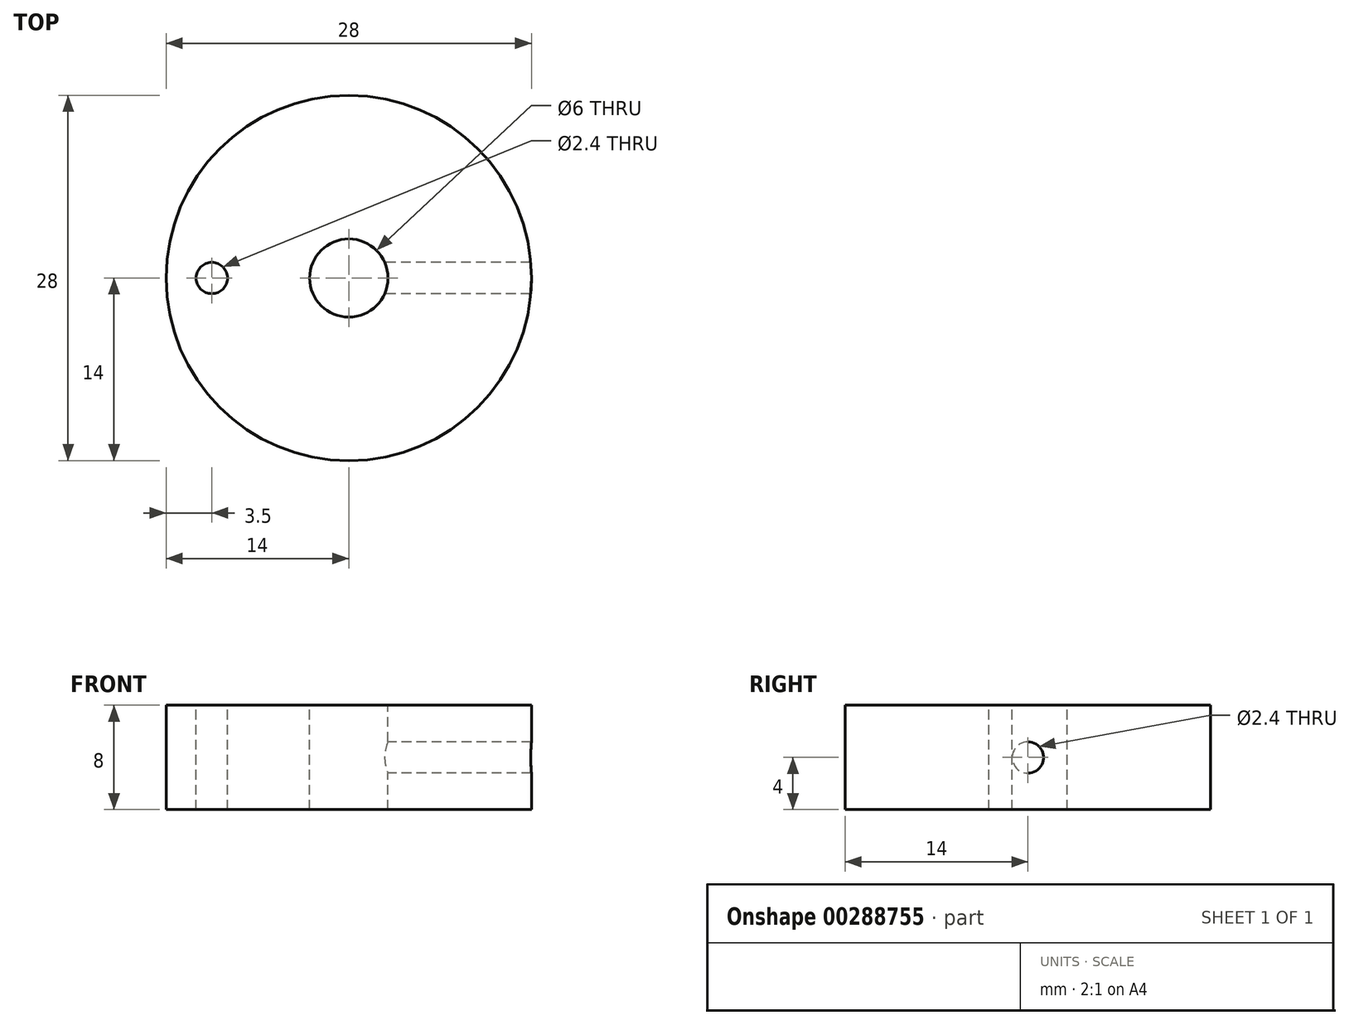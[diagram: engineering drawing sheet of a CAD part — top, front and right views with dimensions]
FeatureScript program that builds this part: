
annotation { "Feature Type Name" : "Feature", "Feature Type Description" : "" }
export const myFeature = defineFeature(function(context is Context, id is Id, definition is map)
    precondition{}
    {
        {
            var Q0;
            Q0=qCreatedBy(makeId("Top.planeOp"),FACE);
            var sketch = newSketch(context, id + "F0", { "sketchPlane" : qUnion([Q0])});
            skCircle(sketch, "E0", {"center": v(0, 0) * mm, "radius": 14 * mm});
            skSolve(sketch);
        }
        {
            var Q0;
            Q0 = qSketchRegion(id + "F0", true);
            extrude(context, id + "F1", {"entities" : qUnion([Q0]), "depth" : 8 * mm});
        }
        {
            var Q0;
            Q0=makeQuery(id+"F1.opExtrude","CAP_FACE",FACE,{"disambiguationData":[OSD([sQuery(id+"F0.wireOp",EDGE,"E0")])],"isStart":false});
            var sketch = newSketch(context, id + "F2", { "sketchPlane" : qUnion([Q0])});
            skPoint(sketch, "E1", {"position": v(0, 0) * mm});
            skPoint(sketch, "E2", {"position": v(-10.5, 0) * mm});
            skSolve(sketch);
        }
        {
            var Q0;
            Q0=sQuery(id+"F2.wireOp",VERTEX,"E1");
            var Q1;
            Q1=makeQuery(id+"F1.opExtrude","SWEPT_BODY",BODY,{"disambiguationData":[OSD([sQuery(id+"F0.wireOp",EDGE,"E0")])]});
            hole(context, id + "F3", {"style" : HoleStyle.SIMPLE, "endStyle" : HoleEndStyle.THROUGH, "holeDiameter" : 6 * mm, "tappedDepth" : 12 * mm, "tapClearance" : 3, "startFromSketch" : true, "locations" : qUnion([Q0]), "scope" : qUnion([Q1])});
        }
        {
            var Q0;
            Q0=sQuery(id+"F2.wireOp",VERTEX,"E2");
            var Q1;
            Q1=makeQuery(id+"F1.opExtrude","SWEPT_BODY",BODY,{"disambiguationData":[OSD([sQuery(id+"F0.wireOp",EDGE,"E0")])]});
            hole(context, id + "F4", {"style" : HoleStyle.SIMPLE, "endStyle" : HoleEndStyle.THROUGH, "standardTappedOrClearance" : lookupTablePath({ "standard" : "ISO", "engagement" : "75%", "pitch" : "0.6 mm", "size" : "M3", "type" : "Tapped" }), "standardBlindInLast" : lookupTablePath({ "standard" : "ISO", "engagement" : "75%", "pitch" : "0.6 mm", "size" : "M3", "type" : "Tapped" }), "holeDiameter" : 2.4 * mm, "showTappedDepth" : true, "tappedDepth" : 12 * mm, "tapClearance" : 3, "startFromSketch" : true, "locations" : qUnion([Q0]), "scope" : qUnion([Q1])});
        }
        {
            var Q0;
            Q0=qCreatedBy(makeId("Right.planeOp"),FACE);
            var sketch = newSketch(context, id + "F5", { "sketchPlane" : qUnion([Q0])});
            skPoint(sketch, "E3", {"position": v(0, 4) * mm});
            skSolve(sketch);
        }
        {
            var Q0;
            Q0=sQuery(id+"F5.wireOp",VERTEX,"E3");
            var Q1;
            Q1=makeQuery(id+"F1.opExtrude","SWEPT_BODY",BODY,{"disambiguationData":[OSD([sQuery(id+"F0.wireOp",EDGE,"E0")])]});
            hole(context, id + "F6", {"style" : HoleStyle.SIMPLE, "endStyle" : HoleEndStyle.THROUGH, "oppositeDirection" : true, "standardTappedOrClearance" : lookupTablePath({ "standard" : "ISO", "engagement" : "75%", "pitch" : "0.6 mm", "size" : "M3", "type" : "Tapped" }), "standardBlindInLast" : lookupTablePath({ "standard" : "ISO", "engagement" : "75%", "pitch" : "0.6 mm", "size" : "M3", "type" : "Tapped" }), "holeDiameter" : 2.4 * mm, "showTappedDepth" : true, "tappedDepth" : 12 * mm, "tapClearance" : 3, "startFromSketch" : true, "locations" : qUnion([Q0]), "scope" : qUnion([Q1])});
        }
    });
